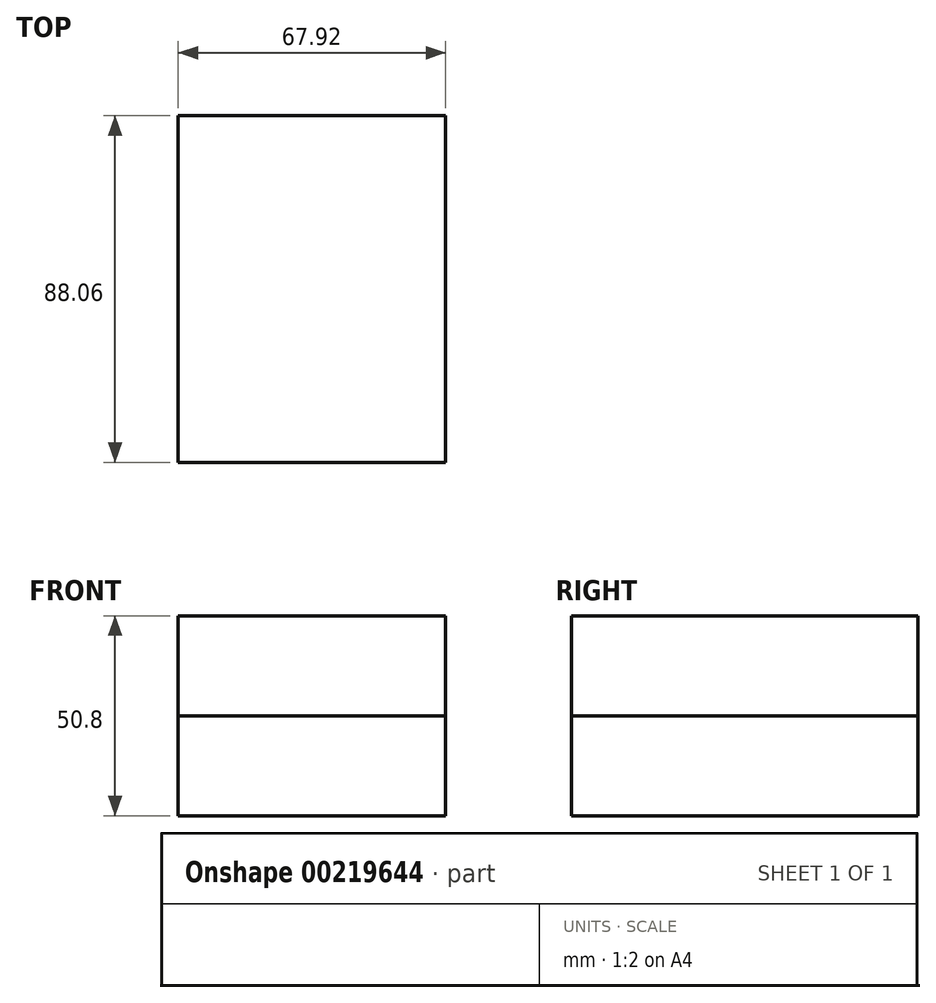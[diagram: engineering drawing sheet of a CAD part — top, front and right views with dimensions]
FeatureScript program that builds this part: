
annotation { "Feature Type Name" : "Feature", "Feature Type Description" : "" }
export const myFeature = defineFeature(function(context is Context, id is Id, definition is map)
    precondition{}
    {
        {
            var Q0;
            Q0=qCreatedBy(makeId("Top.planeOp"),FACE);
            var sketch = newSketch(context, id + "F0", { "sketchPlane" : qUnion([Q0])});
            skLineSegment(sketch, "E0.bottom", {"start": v(33.96, 44.03) * mm, "end": v(-33.96, 44.03) * mm});
            skLineSegment(sketch, "E0.top", {"start": v(33.96, -44.03) * mm, "end": v(-33.96, -44.03) * mm});
            skLineSegment(sketch, "E0.left", {"start": v(33.96, 44.03) * mm, "end": v(33.96, -44.03) * mm});
            skLineSegment(sketch, "E0.right", {"start": v(-33.96, 44.03) * mm, "end": v(-33.96, -44.03) * mm});
            skPoint(sketch, "E0.middle", {"position": v(0, 0) * mm});
            skSolve(sketch);
        }
        {
            var Q0;
            Q0=makeQuery(id+"F0.imprint","IMPRINT",FACE,{"disambiguationData":[TD([[makeQuery(id+"F0.imprint","IMPRINT",EDGE,{"derivedFrom":sQuery(id+"F0.wireOp",EDGE,"E0.bottom")}),1.0]])]});
            extrude(context, id + "F1", {"entities" : qUnion([Q0]), "oppositeDirection" : true, "depth" : 25.4 * mm});
        }
        {
            var Q0;
            Q0=makeQuery(id+"F0.imprint","IMPRINT",FACE,{"disambiguationData":[TD([[makeQuery(id+"F0.imprint","IMPRINT",EDGE,{"derivedFrom":sQuery(id+"F0.wireOp",EDGE,"E0.bottom")}),1.0]])]});
            extrude(context, id + "F2", {"entities" : qUnion([Q0]), "depth" : 25.4 * mm});
        }
    });
